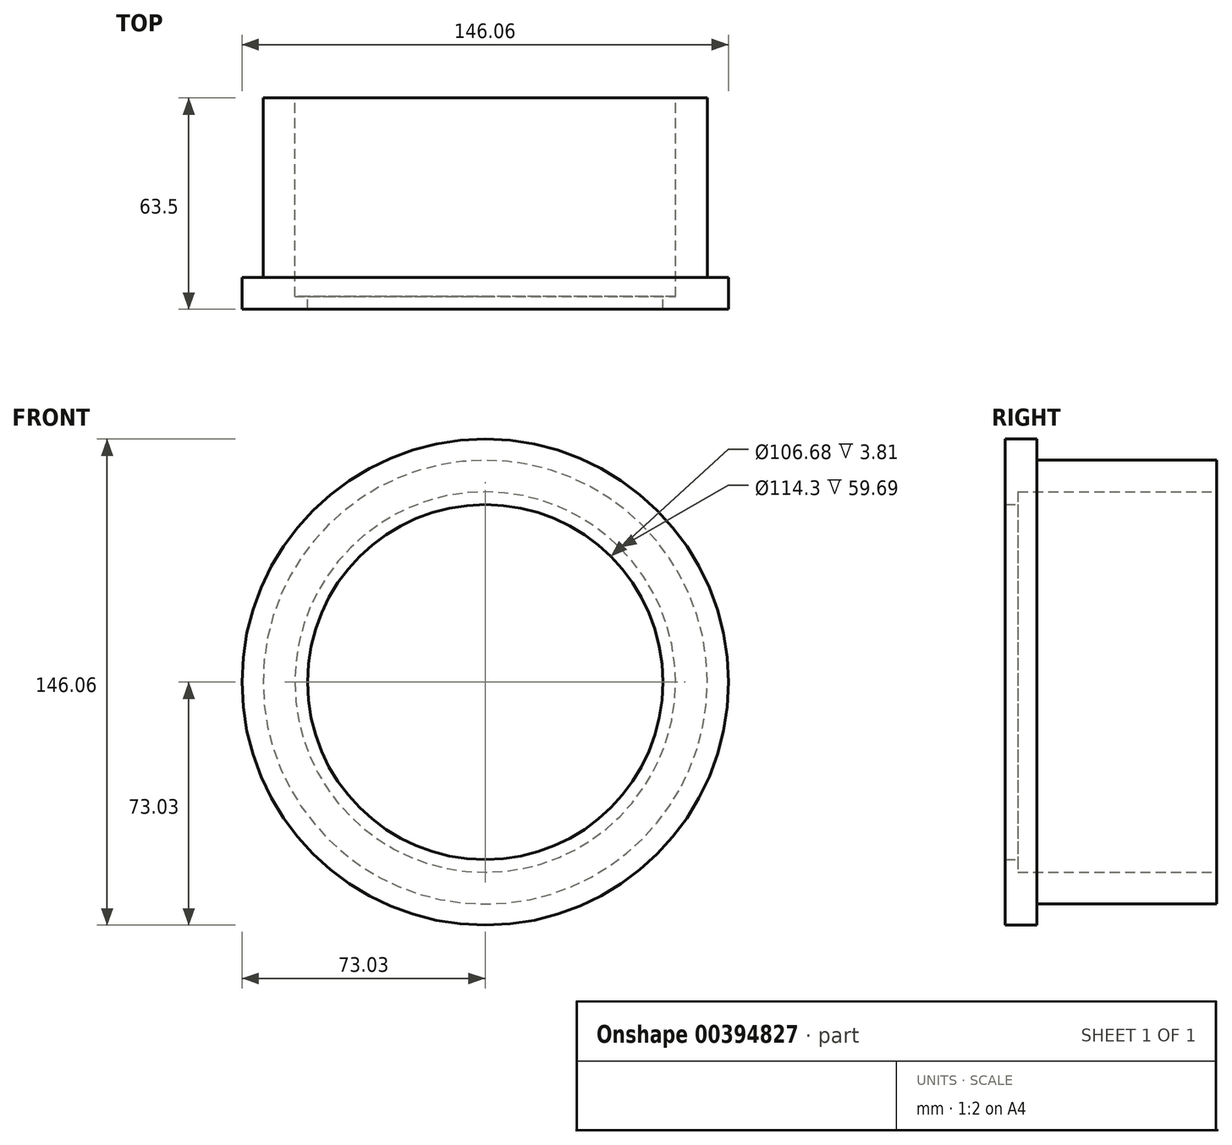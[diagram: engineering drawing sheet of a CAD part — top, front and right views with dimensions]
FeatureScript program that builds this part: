
annotation { "Feature Type Name" : "Feature", "Feature Type Description" : "" }
export const myFeature = defineFeature(function(context is Context, id is Id, definition is map)
    precondition{}
    {
        {
            var Q0;
            Q0=qCreatedBy(makeId("Right.planeOp"),FACE);
            var sketch = newSketch(context, id + "F0", { "sketchPlane" : qUnion([Q0])});
            skLineSegment(sketch, "E0", {"start": v(52.3, 0) * mm, "end": v(-59.41, 0) * mm, "construction": true});
            skLineSegment(sketch, "E1", {"start": v(0, 63.56) * mm, "end": v(0, -63.72) * mm, "construction": true});
            skLineSegment(sketch, "E2", {"start": v(0, 53.34) * mm, "end": v(3.81, 53.34) * mm});
            skLineSegment(sketch, "E3", {"start": v(3.8, 53.34) * mm, "end": v(3.8, 57.15) * mm});
            skLineSegment(sketch, "E4", {"start": v(3.81, 57.15) * mm, "end": v(63.5, 57.15) * mm});
            skLineSegment(sketch, "E5", {"start": v(63.5, 57.15) * mm, "end": v(63.5, 66.68) * mm});
            skLineSegment(sketch, "E6", {"start": v(63.5, 66.68) * mm, "end": v(9.52, 66.68) * mm});
            skLineSegment(sketch, "E7", {"start": v(9.52, 66.68) * mm, "end": v(9.52, 73.03) * mm});
            skLineSegment(sketch, "E8", {"start": v(9.53, 73.03) * mm, "end": v(0, 73.03) * mm});
            skLineSegment(sketch, "E9", {"start": v(0, 73.03) * mm, "end": v(0, 53.34) * mm});
            skSolve(sketch);
        }
        {
            var Q0;
            Q0=qSketchRegion(id+"F0",true);
            var Q1;
            Q1=sQuery(id+"F0.wireOp",EDGE,"E0");
            revolve(context, id + "F1", {"entities" : qUnion([Q0]), "axis" : qUnion([Q1]), "revolveType" : RevolveType.FULL});
        }
    });
